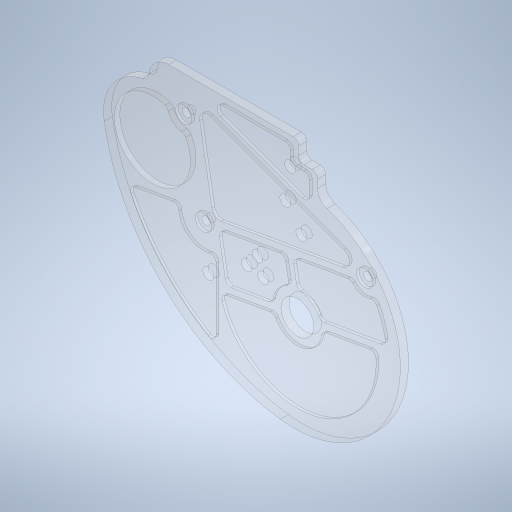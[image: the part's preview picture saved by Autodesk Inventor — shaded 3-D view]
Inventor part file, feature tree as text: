
AUTODESK INVENTOR PART (.ipt)
format: ipt  version: 2023.1 (Build 271208000, 208)  size: 467,456 bytes
history: native  units: mm
features: other x3, sketch x2
ambient origin geometry x8: Origin, YZ Plane, XZ Plane, XY Plane, X Axis, Y Axis, Z Axis, Center Point
bodies: Solid2 (feature_tree)
feature tree (5):
  other  "足外フレーム.ipt"
  other  "Solid2::足外フレーム.ipt"
  other  "TaggingFeature1"
  sketch  "Sketch6"  dims[d0=10.0mm]
  sketch  "Sketch10"
